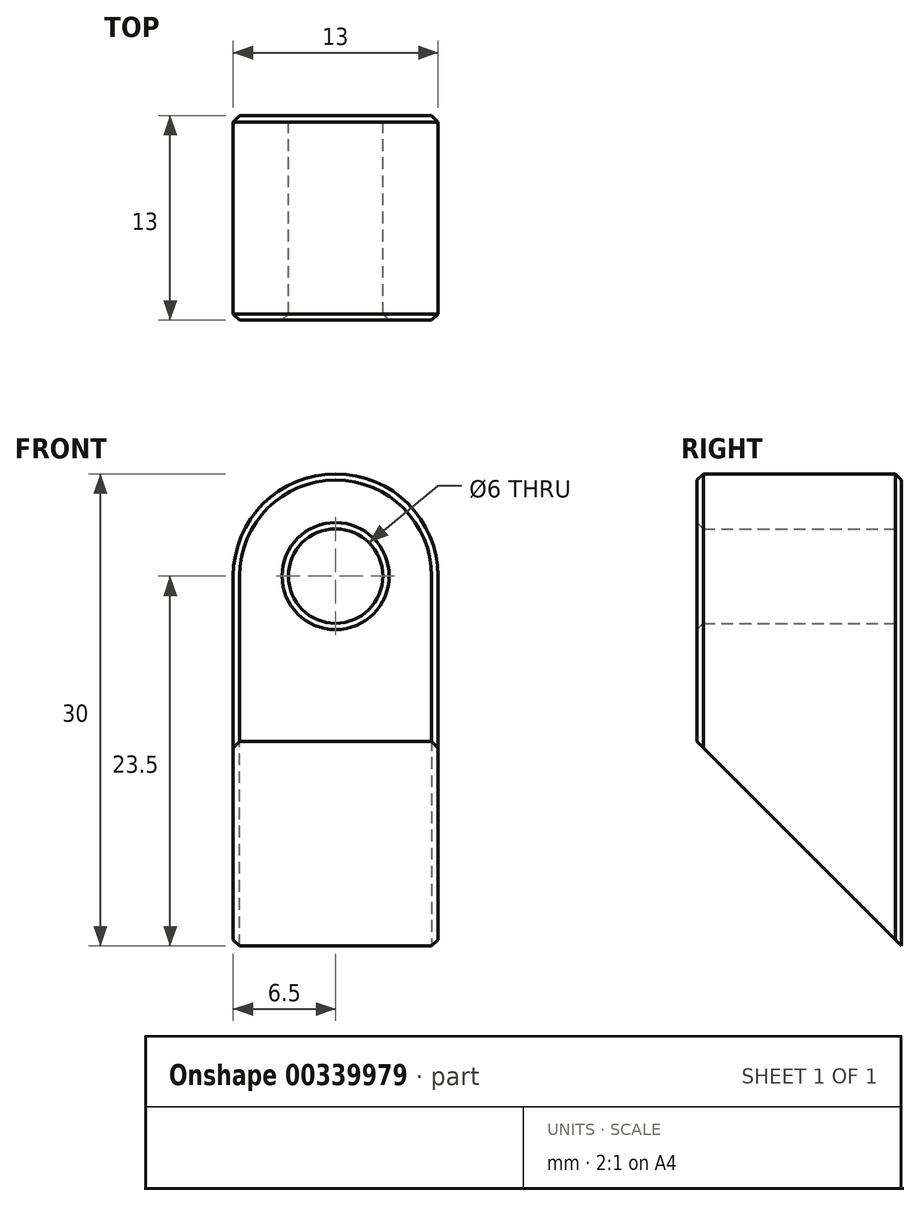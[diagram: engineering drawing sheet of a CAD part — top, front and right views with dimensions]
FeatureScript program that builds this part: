
annotation { "Feature Type Name" : "Feature", "Feature Type Description" : "" }
export const myFeature = defineFeature(function(context is Context, id is Id, definition is map)
    precondition{}
    {
        {
            var Q0;
            Q0=qCreatedBy(makeId("Top.planeOp"),FACE);
            var sketch = newSketch(context, id + "F0", { "sketchPlane" : qUnion([Q0])});
            skLineSegment(sketch, "E0.bottom", {"start": v(6.5, -6.5) * mm, "end": v(-6.5, -6.5) * mm});
            skLineSegment(sketch, "E0.top", {"start": v(6.5, 6.5) * mm, "end": v(-6.5, 6.5) * mm});
            skLineSegment(sketch, "E0.left", {"start": v(6.5, -6.5) * mm, "end": v(6.5, 6.5) * mm});
            skLineSegment(sketch, "E0.right", {"start": v(-6.5, -6.5) * mm, "end": v(-6.5, 6.5) * mm});
            skPoint(sketch, "E0.middle", {"position": v(0, 0) * mm});
            skSolve(sketch);
        }
        {
            var Q0;
            Q0 = qSketchRegion(id + "F0", true);
            extrude(context, id + "F1", {"entities" : qUnion([Q0]), "depth" : 30 * mm});
        }
        {
            var Q0;
            Q0=makeQuery(id+"F1.opExtrude","CAP_EDGE",EDGE,{"disambiguationData":[OSD([sQuery(id+"F0.wireOp",EDGE,"E0.bottom")])],"isStart":true});
            chamfer(context, id + "F2", {"entities" : qUnion([Q0]), "width" : 13 * mm, "tangentPropagation" : true});
        }
        {
            var Q0;
            Q0=makeQuery(id+"F1.opExtrude","CAP_EDGE",EDGE,{"disambiguationData":[OSD([sQuery(id+"F0.wireOp",EDGE,"E0.left")])],"isStart":false});
            var Q1;
            Q1=makeQuery(id+"F1.opExtrude","CAP_EDGE",EDGE,{"disambiguationData":[OSD([sQuery(id+"F0.wireOp",EDGE,"E0.right")])],"isStart":false});
            fillet(context, id + "F3", {"entities" : qUnion([Q0, Q1]), "radius" : 6.5 * mm, "tangentPropagation" : true, "allowEdgeOverflow" : false});
        }
        {
            var Q0;
            Q0=makeQuery(id+"F1.opExtrude","SWEPT_FACE",FACE,{"disambiguationData":[OSD([sQuery(id+"F0.wireOp",EDGE,"E0.top")])]});
            var sketch = newSketch(context, id + "F4", { "sketchPlane" : qUnion([Q0])});
            skCircle(sketch, "E1", {"center": v(0, 23.5) * mm, "radius": 3 * mm});
            skSolve(sketch);
        }
        {
            var Q0;
            Q0 = qSketchRegion(id + "F4", true);
            extrude(context, id + "F5", {"entities" : qUnion([Q0]), "operationType" : NewBodyOperationType.REMOVE, "oppositeDirection" : true, "depth" : 25 * mm});
        }
        {
            var Q0;
            Q0=makeQuery(id+"F3.opFillet","BLEND_EDGE",EDGE,{"blendedFrom":[makeQuery(id+"F1.opExtrude","CAP_EDGE",EDGE,{"disambiguationData":[OSD([sQuery(id+"F0.wireOp",EDGE,"E0.left")])],"isStart":false}),makeQuery(id+"F1.opExtrude","SWEPT_FACE",FACE,{"disambiguationData":[OSD([sQuery(id+"F0.wireOp",EDGE,"E0.top")])]})],"blendedInto":[makeQuery(id+"F1.opExtrude","SWEPT_FACE",FACE,{"disambiguationData":[OSD([sQuery(id+"F0.wireOp",EDGE,"E0.top")])]})]});
            var Q1;
            Q1=makeQuery(id+"F3.opFillet","BLEND_EDGE",EDGE,{"blendedFrom":[makeQuery(id+"F1.opExtrude","CAP_EDGE",EDGE,{"disambiguationData":[OSD([sQuery(id+"F0.wireOp",EDGE,"E0.left")])],"isStart":false}),makeQuery(id+"F1.opExtrude","SWEPT_FACE",FACE,{"disambiguationData":[OSD([sQuery(id+"F0.wireOp",EDGE,"E0.bottom")])]})],"blendedInto":[makeQuery(id+"F1.opExtrude","SWEPT_FACE",FACE,{"disambiguationData":[OSD([sQuery(id+"F0.wireOp",EDGE,"E0.bottom")])]})]});
            var Q2;
            Q2=makeQuery(id+"F5.boolean.opBoolean","COPY",EDGE,{"derivedFrom":makeQuery(id+"F5.opExtrude","CAP_EDGE",EDGE,{"disambiguationData":[OSD([sQuery(id+"F4.wireOp",EDGE,"E1")])],"isStart":true})});
            var Q3;
            Q3=makeQuery(id+"F5.boolean.opBoolean","INTERSECT",EDGE,{"derivedFrom":[makeQuery(id+"F1.opExtrude","SWEPT_FACE",FACE,{"disambiguationData":[OSD([sQuery(id+"F0.wireOp",EDGE,"E0.bottom")])]}),makeQuery(id+"F5.opExtrude","SWEPT_FACE",FACE,{"disambiguationData":[OSD([sQuery(id+"F4.wireOp",EDGE,"E1")])]})]});
            chamfer(context, id + "F6", {"entities" : qUnion([Q0, Q1, Q2, Q3]), "width" : 0.4 * mm, "tangentPropagation" : true});
        }
    });
